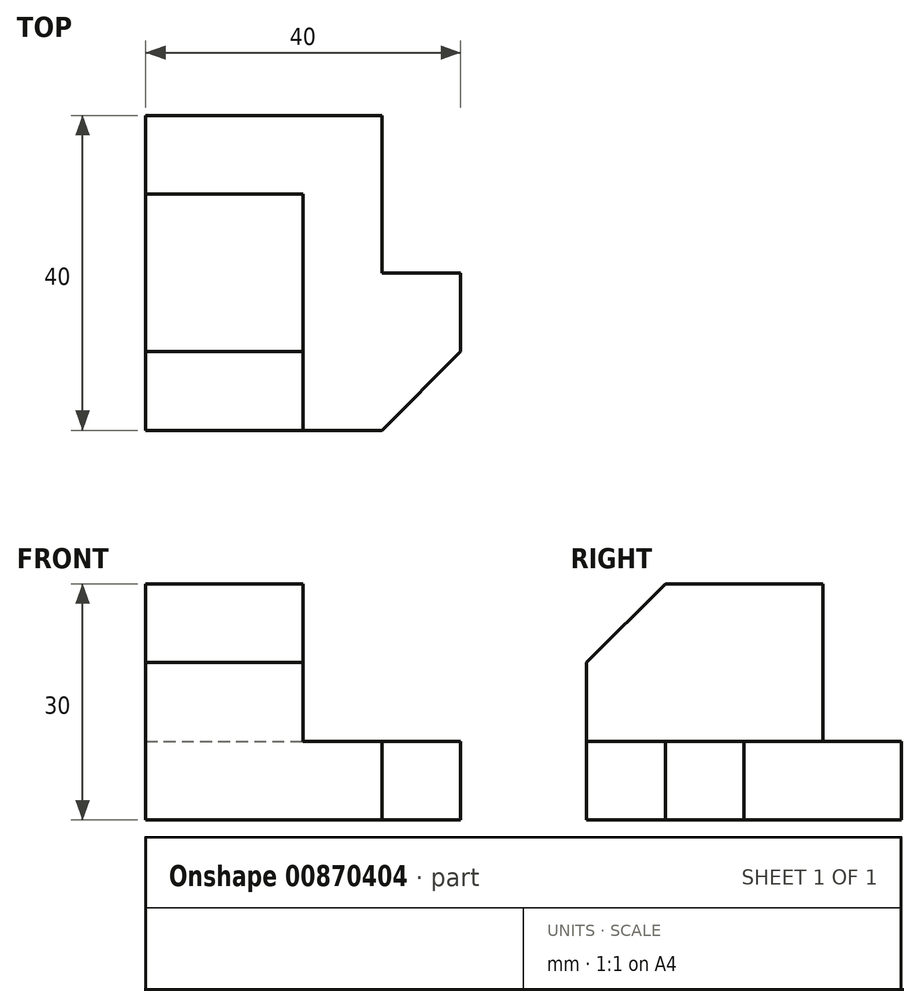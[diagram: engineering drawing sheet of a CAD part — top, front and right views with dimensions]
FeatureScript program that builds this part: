
annotation { "Feature Type Name" : "Feature", "Feature Type Description" : "" }
export const myFeature = defineFeature(function(context is Context, id is Id, definition is map)
    precondition{}
    {
        {
            var Q0;
            Q0=qCreatedBy(makeId("Top.planeOp"),FACE);
            var sketch = newSketch(context, id + "F0", { "sketchPlane" : qUnion([Q0])});
            skLineSegment(sketch, "E0", {"start": v(0, 0) * mm, "end": v(0, 40) * mm});
            skLineSegment(sketch, "E1", {"start": v(0, 40) * mm, "end": v(30, 40) * mm});
            skLineSegment(sketch, "E2", {"start": v(30, 40) * mm, "end": v(30, 20) * mm});
            skLineSegment(sketch, "E3", {"start": v(30, 20) * mm, "end": v(40, 20) * mm});
            skLineSegment(sketch, "E4", {"start": v(40, 20) * mm, "end": v(40, 10) * mm});
            skLineSegment(sketch, "E5", {"start": v(40, 10) * mm, "end": v(30, 0) * mm});
            skLineSegment(sketch, "E6", {"start": v(30, 0) * mm, "end": v(0, 0) * mm});
            skSolve(sketch);
        }
        {
            var Q0;
            Q0 = qSketchRegion(id + "F0", true);
            extrude(context, id + "F1", {"entities" : qUnion([Q0]), "depth" : 10 * mm, "offsetDistance" : 25 * mm});
        }
        {
            var Q0;
            Q0=makeQuery(id+"F1.opExtrude","CAP_FACE",FACE,{"disambiguationData":[OSD([sQuery(id+"F0.wireOp",EDGE,"E0"),sQuery(id+"F0.wireOp",EDGE,"E1"),sQuery(id+"F0.wireOp",EDGE,"E2"),sQuery(id+"F0.wireOp",EDGE,"E3"),sQuery(id+"F0.wireOp",EDGE,"E4"),sQuery(id+"F0.wireOp",EDGE,"E5"),sQuery(id+"F0.wireOp",EDGE,"E6")])],"isStart":false});
            var sketch = newSketch(context, id + "F2", { "sketchPlane" : qUnion([Q0])});
            skLineSegment(sketch, "E7.bottom", {"start": v(0, 0) * mm, "end": v(20, 0) * mm});
            skLineSegment(sketch, "E7.top", {"start": v(0, 30) * mm, "end": v(20, 30) * mm});
            skLineSegment(sketch, "E7.left", {"start": v(0, 0) * mm, "end": v(0, 30) * mm});
            skLineSegment(sketch, "E7.right", {"start": v(20, 0) * mm, "end": v(20, 30) * mm});
            skSolve(sketch);
        }
        {
            var Q0;
            Q0 = qSketchRegion(id + "F2", true);
            extrude(context, id + "F3", {"entities" : qUnion([Q0]), "operationType" : NewBodyOperationType.ADD, "depth" : 20 * mm, "offsetDistance" : 25 * mm});
        }
        {
            var Q0;
            Q0=makeQuery(id+"F3.opExtrude","CAP_EDGE",EDGE,{"disambiguationData":[OSD([sQuery(id+"F2.wireOp",EDGE,"E7.bottom")])],"isStart":false});
            chamfer(context, id + "F4", {"entities" : qUnion([Q0]), "width" : 10 * mm, "tangentPropagation" : true});
        }
    });
